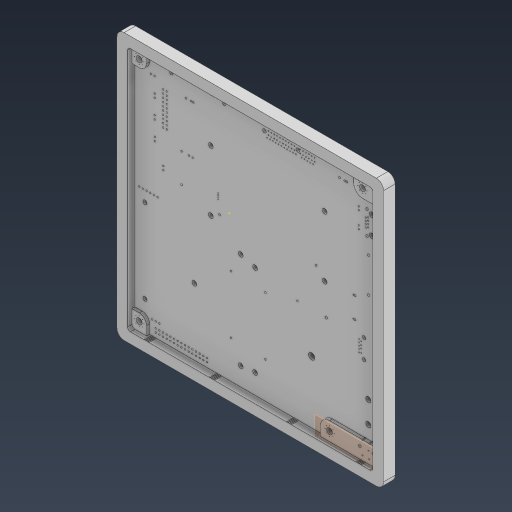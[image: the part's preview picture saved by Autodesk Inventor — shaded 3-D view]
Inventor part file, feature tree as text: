
AUTODESK INVENTOR PART (.ipt)
format: ipt  version: 2024.2 (Build 282272000, 272)  size: 747,008 bytes
history: native  units: mm
features: other x3, plane x1, sketch x1
ambient origin geometry x8: Origin, YZ Plane, XZ Plane, XY Plane, X Axis, Y Axis, Z Axis, Center Point
bodies: Body1 (feature_tree)
feature tree (5):
  other  "base.ipt"
  plane  "工作平面1"
  sketch  "草圖3"
  other  "實體2690::base.ipt"
  other  "標籤特徵1"
